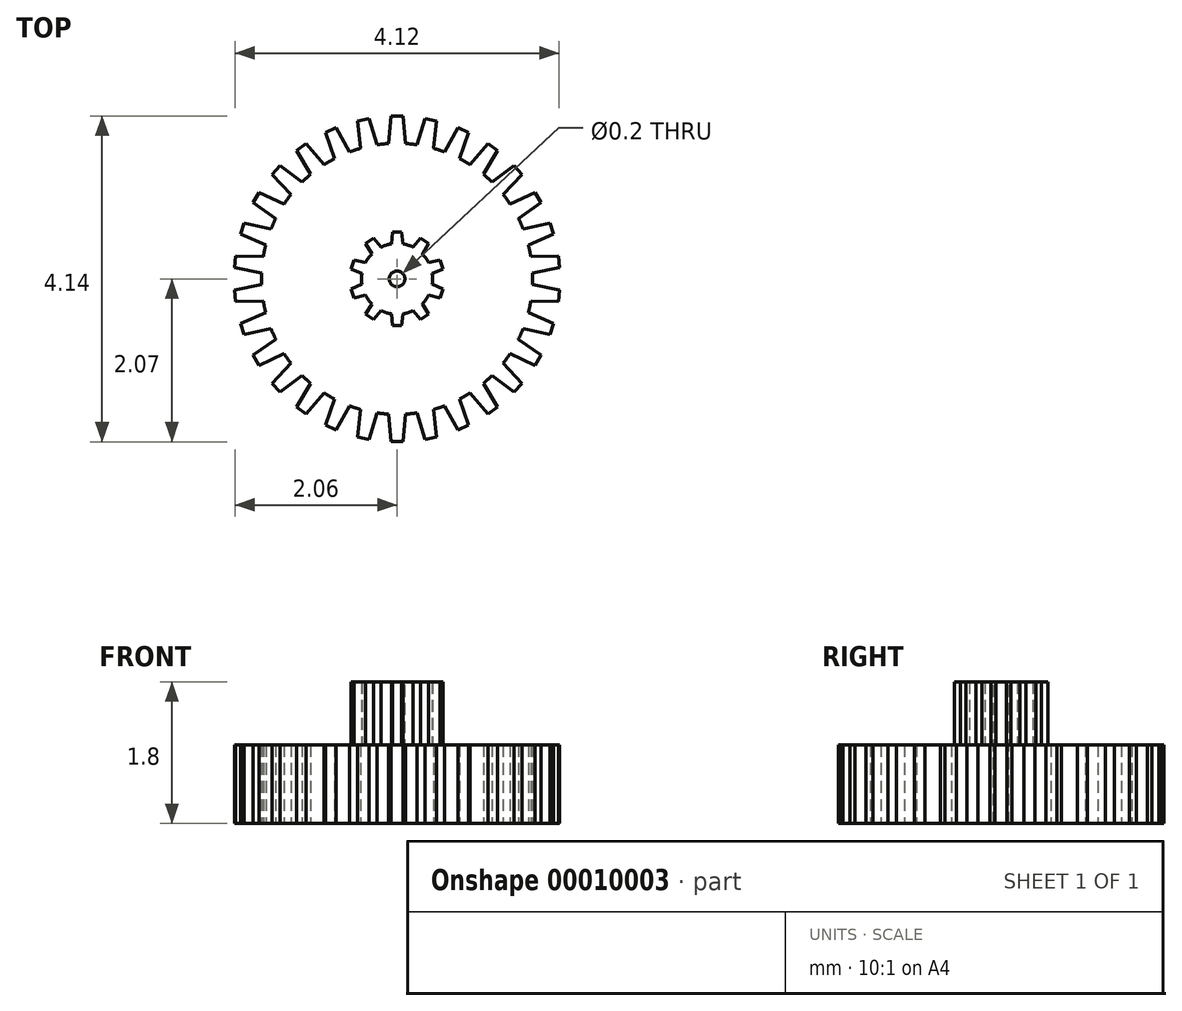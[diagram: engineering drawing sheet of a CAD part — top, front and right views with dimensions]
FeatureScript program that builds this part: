
annotation { "Feature Type Name" : "Feature", "Feature Type Description" : "" }
export const myFeature = defineFeature(function(context is Context, id is Id, definition is map)
    precondition{}
    {
        {
            var Q0;
            Q0=qCreatedBy(makeId("Top.planeOp"),FACE);
            var sketch = newSketch(context, id + "F0", { "sketchPlane" : qUnion([Q0])});
            skCircle(sketch, "E0", {"center": v(0, 0) * mm, "radius": 1.72 * mm});
            skLineSegment(sketch, "E1", {"start": v(0, 0) * mm, "end": v(0, 1.72) * mm, "construction": true});
            skLineSegment(sketch, "E2", {"start": v(-0.1, 1.72) * mm, "end": v(-0.08, 2.07) * mm});
            skLineSegment(sketch, "E3", {"start": v(-0.07, 2.07) * mm, "end": v(0, 2.07) * mm});
            skLineSegment(sketch, "E4.0.MirrorCS", {"start": v(0.07, 2.07) * mm, "end": v(0, 2.07) * mm});
            skLineSegment(sketch, "E5.0.MirrorCS", {"start": v(0.1, 1.72) * mm, "end": v(0.08, 2.07) * mm});
            skLineSegment(sketch, "E6.1.0", {"start": v(-0.46, 1.66) * mm, "end": v(-0.5, 2) * mm});
            skLineSegment(sketch, "E6.1.1", {"start": v(-0.5, 2) * mm, "end": v(-0.43, 2.02) * mm});
            skLineSegment(sketch, "E6.1.2", {"start": v(-0.36, 2.04) * mm, "end": v(-0.43, 2.02) * mm});
            skLineSegment(sketch, "E6.1.3", {"start": v(-0.25, 1.7) * mm, "end": v(-0.36, 2.04) * mm});
            skLineSegment(sketch, "E6.2.0", {"start": v(-0.8, 1.53) * mm, "end": v(-0.9, 1.86) * mm});
            skLineSegment(sketch, "E6.2.1", {"start": v(-0.9, 1.86) * mm, "end": v(-0.84, 1.89) * mm});
            skLineSegment(sketch, "E6.2.2", {"start": v(-0.77, 1.92) * mm, "end": v(-0.84, 1.89) * mm});
            skLineSegment(sketch, "E6.2.3", {"start": v(-0.6, 1.61) * mm, "end": v(-0.77, 1.92) * mm});
            skLineSegment(sketch, "E6.3.0", {"start": v(-1.1, 1.33) * mm, "end": v(-1.28, 1.63) * mm});
            skLineSegment(sketch, "E6.3.1", {"start": v(-1.28, 1.63) * mm, "end": v(-1.22, 1.67) * mm});
            skLineSegment(sketch, "E6.3.2", {"start": v(-1.15, 1.72) * mm, "end": v(-1.22, 1.67) * mm});
            skLineSegment(sketch, "E6.3.3", {"start": v(-0.92, 1.45) * mm, "end": v(-1.15, 1.72) * mm});
            skLineSegment(sketch, "E6.4.0", {"start": v(-1.35, 1.07) * mm, "end": v(-1.59, 1.33) * mm});
            skLineSegment(sketch, "E6.4.1", {"start": v(-1.59, 1.33) * mm, "end": v(-1.54, 1.38) * mm});
            skLineSegment(sketch, "E6.4.2", {"start": v(-1.49, 1.44) * mm, "end": v(-1.54, 1.38) * mm});
            skLineSegment(sketch, "E6.4.3", {"start": v(-1.2, 1.23) * mm, "end": v(-1.49, 1.44) * mm});
            skLineSegment(sketch, "E6.5.0", {"start": v(-1.54, 0.77) * mm, "end": v(-1.83, 0.97) * mm});
            skLineSegment(sketch, "E6.5.1", {"start": v(-1.83, 0.97) * mm, "end": v(-1.8, 1.03) * mm});
            skLineSegment(sketch, "E6.5.2", {"start": v(-1.75, 1.1) * mm, "end": v(-1.8, 1.03) * mm});
            skLineSegment(sketch, "E6.5.3", {"start": v(-1.44, 0.95) * mm, "end": v(-1.75, 1.1) * mm});
            skLineSegment(sketch, "E6.6.0", {"start": v(-1.67, 0.43) * mm, "end": v(-1.99, 0.57) * mm});
            skLineSegment(sketch, "E6.6.1", {"start": v(-1.99, 0.57) * mm, "end": v(-1.97, 0.64) * mm});
            skLineSegment(sketch, "E6.6.2", {"start": v(-1.94, 0.71) * mm, "end": v(-1.97, 0.64) * mm});
            skLineSegment(sketch, "E6.6.3", {"start": v(-1.6, 0.63) * mm, "end": v(-1.94, 0.71) * mm});
            skLineSegment(sketch, "E6.7.0", {"start": v(-1.72, 0.07) * mm, "end": v(-2.06, 0.14) * mm});
            skLineSegment(sketch, "E6.7.1", {"start": v(-2.06, 0.14) * mm, "end": v(-2.06, 0.22) * mm});
            skLineSegment(sketch, "E6.7.2", {"start": v(-2.05, 0.3) * mm, "end": v(-2.06, 0.22) * mm});
            skLineSegment(sketch, "E6.7.3", {"start": v(-1.7, 0.28) * mm, "end": v(-2.05, 0.3) * mm});
            skLineSegment(sketch, "E6.8.0", {"start": v(-1.7, -0.28) * mm, "end": v(-2.05, -0.3) * mm});
            skLineSegment(sketch, "E6.8.1", {"start": v(-2.05, -0.3) * mm, "end": v(-2.06, -0.22) * mm});
            skLineSegment(sketch, "E6.8.2", {"start": v(-2.06, -0.14) * mm, "end": v(-2.06, -0.22) * mm});
            skLineSegment(sketch, "E6.8.3", {"start": v(-1.72, -0.07) * mm, "end": v(-2.06, -0.14) * mm});
            skLineSegment(sketch, "E6.9.0", {"start": v(-1.6, -0.63) * mm, "end": v(-1.94, -0.71) * mm});
            skLineSegment(sketch, "E6.9.1", {"start": v(-1.94, -0.71) * mm, "end": v(-1.97, -0.64) * mm});
            skLineSegment(sketch, "E6.9.2", {"start": v(-1.99, -0.57) * mm, "end": v(-1.97, -0.64) * mm});
            skLineSegment(sketch, "E6.9.3", {"start": v(-1.67, -0.43) * mm, "end": v(-1.99, -0.57) * mm});
            skLineSegment(sketch, "E6.10.0", {"start": v(-1.44, -0.95) * mm, "end": v(-1.75, -1.1) * mm});
            skLineSegment(sketch, "E6.10.1", {"start": v(-1.75, -1.1) * mm, "end": v(-1.8, -1.03) * mm});
            skLineSegment(sketch, "E6.10.2", {"start": v(-1.83, -0.97) * mm, "end": v(-1.8, -1.03) * mm});
            skLineSegment(sketch, "E6.10.3", {"start": v(-1.54, -0.77) * mm, "end": v(-1.83, -0.97) * mm});
            skLineSegment(sketch, "E6.11.0", {"start": v(-1.2, -1.23) * mm, "end": v(-1.49, -1.44) * mm});
            skLineSegment(sketch, "E6.11.1", {"start": v(-1.49, -1.44) * mm, "end": v(-1.54, -1.38) * mm});
            skLineSegment(sketch, "E6.11.2", {"start": v(-1.59, -1.33) * mm, "end": v(-1.54, -1.38) * mm});
            skLineSegment(sketch, "E6.11.3", {"start": v(-1.35, -1.07) * mm, "end": v(-1.59, -1.33) * mm});
            skLineSegment(sketch, "E6.12.0", {"start": v(-0.92, -1.45) * mm, "end": v(-1.15, -1.72) * mm});
            skLineSegment(sketch, "E6.12.1", {"start": v(-1.15, -1.72) * mm, "end": v(-1.22, -1.67) * mm});
            skLineSegment(sketch, "E6.12.2", {"start": v(-1.28, -1.63) * mm, "end": v(-1.22, -1.67) * mm});
            skLineSegment(sketch, "E6.12.3", {"start": v(-1.1, -1.33) * mm, "end": v(-1.28, -1.63) * mm});
            skLineSegment(sketch, "E6.13.0", {"start": v(-0.6, -1.61) * mm, "end": v(-0.77, -1.92) * mm});
            skLineSegment(sketch, "E6.13.1", {"start": v(-0.77, -1.92) * mm, "end": v(-0.84, -1.89) * mm});
            skLineSegment(sketch, "E6.13.2", {"start": v(-0.9, -1.86) * mm, "end": v(-0.84, -1.89) * mm});
            skLineSegment(sketch, "E6.13.3", {"start": v(-0.8, -1.53) * mm, "end": v(-0.9, -1.86) * mm});
            skLineSegment(sketch, "E6.14.0", {"start": v(-0.25, -1.7) * mm, "end": v(-0.36, -2.04) * mm});
            skLineSegment(sketch, "E6.14.1", {"start": v(-0.36, -2.04) * mm, "end": v(-0.43, -2.02) * mm});
            skLineSegment(sketch, "E6.14.2", {"start": v(-0.5, -2) * mm, "end": v(-0.43, -2.02) * mm});
            skLineSegment(sketch, "E6.14.3", {"start": v(-0.46, -1.66) * mm, "end": v(-0.5, -2) * mm});
            skLineSegment(sketch, "E6.15.0", {"start": v(0.1, -1.72) * mm, "end": v(0.08, -2.07) * mm});
            skLineSegment(sketch, "E6.15.1", {"start": v(0.07, -2.07) * mm, "end": v(0, -2.07) * mm});
            skLineSegment(sketch, "E6.15.2", {"start": v(-0.07, -2.07) * mm, "end": v(0, -2.07) * mm});
            skLineSegment(sketch, "E6.15.3", {"start": v(-0.1, -1.72) * mm, "end": v(-0.08, -2.07) * mm});
            skLineSegment(sketch, "E6.16.0", {"start": v(0.46, -1.66) * mm, "end": v(0.5, -2) * mm});
            skLineSegment(sketch, "E6.16.1", {"start": v(0.5, -2) * mm, "end": v(0.43, -2.02) * mm});
            skLineSegment(sketch, "E6.16.2", {"start": v(0.36, -2.04) * mm, "end": v(0.43, -2.02) * mm});
            skLineSegment(sketch, "E6.16.3", {"start": v(0.25, -1.7) * mm, "end": v(0.36, -2.04) * mm});
            skLineSegment(sketch, "E6.17.0", {"start": v(0.8, -1.53) * mm, "end": v(0.9, -1.86) * mm});
            skLineSegment(sketch, "E6.17.1", {"start": v(0.9, -1.86) * mm, "end": v(0.84, -1.89) * mm});
            skLineSegment(sketch, "E6.17.2", {"start": v(0.77, -1.92) * mm, "end": v(0.84, -1.89) * mm});
            skLineSegment(sketch, "E6.17.3", {"start": v(0.6, -1.61) * mm, "end": v(0.77, -1.92) * mm});
            skLineSegment(sketch, "E6.18.0", {"start": v(1.1, -1.33) * mm, "end": v(1.28, -1.63) * mm});
            skLineSegment(sketch, "E6.18.1", {"start": v(1.28, -1.63) * mm, "end": v(1.22, -1.67) * mm});
            skLineSegment(sketch, "E6.18.2", {"start": v(1.15, -1.72) * mm, "end": v(1.22, -1.67) * mm});
            skLineSegment(sketch, "E6.18.3", {"start": v(0.92, -1.45) * mm, "end": v(1.15, -1.72) * mm});
            skLineSegment(sketch, "E6.19.0", {"start": v(1.35, -1.07) * mm, "end": v(1.59, -1.33) * mm});
            skLineSegment(sketch, "E6.19.1", {"start": v(1.59, -1.33) * mm, "end": v(1.54, -1.38) * mm});
            skLineSegment(sketch, "E6.19.2", {"start": v(1.49, -1.44) * mm, "end": v(1.54, -1.38) * mm});
            skLineSegment(sketch, "E6.19.3", {"start": v(1.2, -1.23) * mm, "end": v(1.49, -1.44) * mm});
            skLineSegment(sketch, "E6.20.0", {"start": v(1.54, -0.77) * mm, "end": v(1.83, -0.97) * mm});
            skLineSegment(sketch, "E6.20.1", {"start": v(1.83, -0.97) * mm, "end": v(1.8, -1.03) * mm});
            skLineSegment(sketch, "E6.20.2", {"start": v(1.75, -1.1) * mm, "end": v(1.8, -1.03) * mm});
            skLineSegment(sketch, "E6.20.3", {"start": v(1.44, -0.95) * mm, "end": v(1.75, -1.1) * mm});
            skLineSegment(sketch, "E7", {"start": v(0, 0) * mm, "end": v(0, 0.43) * mm, "construction": true});
            skLineSegment(sketch, "E8.1.21.0", {"start": v(1.67, -0.43) * mm, "end": v(1.99, -0.57) * mm});
            skLineSegment(sketch, "E8.3.21.0", {"start": v(1.99, -0.57) * mm, "end": v(1.97, -0.64) * mm});
            skLineSegment(sketch, "E8.6.21.0", {"start": v(1.94, -0.71) * mm, "end": v(1.97, -0.64) * mm});
            skLineSegment(sketch, "E8.9.21.0", {"start": v(1.6, -0.63) * mm, "end": v(1.94, -0.71) * mm});
            skLineSegment(sketch, "E8.1.22.0", {"start": v(1.72, -0.07) * mm, "end": v(2.06, -0.14) * mm});
            skLineSegment(sketch, "E8.3.22.0", {"start": v(2.06, -0.14) * mm, "end": v(2.06, -0.22) * mm});
            skLineSegment(sketch, "E8.6.22.0", {"start": v(2.05, -0.3) * mm, "end": v(2.06, -0.22) * mm});
            skLineSegment(sketch, "E8.9.22.0", {"start": v(1.7, -0.28) * mm, "end": v(2.05, -0.3) * mm});
            skLineSegment(sketch, "E8.1.23.0", {"start": v(1.7, 0.28) * mm, "end": v(2.05, 0.3) * mm});
            skLineSegment(sketch, "E8.3.23.0", {"start": v(2.05, 0.3) * mm, "end": v(2.06, 0.22) * mm});
            skLineSegment(sketch, "E8.6.23.0", {"start": v(2.06, 0.14) * mm, "end": v(2.06, 0.22) * mm});
            skLineSegment(sketch, "E8.9.23.0", {"start": v(1.72, 0.07) * mm, "end": v(2.06, 0.14) * mm});
            skLineSegment(sketch, "E9.1.24.0", {"start": v(1.6, 0.63) * mm, "end": v(1.94, 0.71) * mm});
            skLineSegment(sketch, "E9.3.24.0", {"start": v(1.94, 0.71) * mm, "end": v(1.97, 0.64) * mm});
            skLineSegment(sketch, "E9.6.24.0", {"start": v(1.99, 0.57) * mm, "end": v(1.97, 0.64) * mm});
            skLineSegment(sketch, "E9.9.24.0", {"start": v(1.67, 0.43) * mm, "end": v(1.99, 0.57) * mm});
            skLineSegment(sketch, "E9.1.25.0", {"start": v(1.44, 0.95) * mm, "end": v(1.75, 1.1) * mm});
            skLineSegment(sketch, "E9.3.25.0", {"start": v(1.75, 1.1) * mm, "end": v(1.8, 1.03) * mm});
            skLineSegment(sketch, "E9.6.25.0", {"start": v(1.83, 0.97) * mm, "end": v(1.8, 1.03) * mm});
            skLineSegment(sketch, "E9.9.25.0", {"start": v(1.54, 0.77) * mm, "end": v(1.83, 0.97) * mm});
            skLineSegment(sketch, "E9.1.26.0", {"start": v(1.2, 1.23) * mm, "end": v(1.49, 1.44) * mm});
            skLineSegment(sketch, "E9.3.26.0", {"start": v(1.49, 1.44) * mm, "end": v(1.54, 1.38) * mm});
            skLineSegment(sketch, "E9.6.26.0", {"start": v(1.59, 1.33) * mm, "end": v(1.54, 1.38) * mm});
            skLineSegment(sketch, "E9.9.26.0", {"start": v(1.35, 1.07) * mm, "end": v(1.59, 1.33) * mm});
            skLineSegment(sketch, "E9.1.27.0", {"start": v(0.92, 1.45) * mm, "end": v(1.15, 1.72) * mm});
            skLineSegment(sketch, "E9.3.27.0", {"start": v(1.15, 1.72) * mm, "end": v(1.22, 1.67) * mm});
            skLineSegment(sketch, "E9.6.27.0", {"start": v(1.28, 1.63) * mm, "end": v(1.22, 1.67) * mm});
            skLineSegment(sketch, "E9.9.27.0", {"start": v(1.1, 1.33) * mm, "end": v(1.28, 1.63) * mm});
            skLineSegment(sketch, "E9.1.28.0", {"start": v(0.6, 1.61) * mm, "end": v(0.77, 1.92) * mm});
            skLineSegment(sketch, "E9.3.28.0", {"start": v(0.77, 1.92) * mm, "end": v(0.84, 1.89) * mm});
            skLineSegment(sketch, "E9.6.28.0", {"start": v(0.9, 1.86) * mm, "end": v(0.84, 1.89) * mm});
            skLineSegment(sketch, "E9.9.28.0", {"start": v(0.8, 1.53) * mm, "end": v(0.9, 1.86) * mm});
            skLineSegment(sketch, "E9.1.29.0", {"start": v(0.25, 1.7) * mm, "end": v(0.36, 2.04) * mm});
            skLineSegment(sketch, "E9.3.29.0", {"start": v(0.36, 2.04) * mm, "end": v(0.43, 2.02) * mm});
            skLineSegment(sketch, "E9.6.29.0", {"start": v(0.5, 2) * mm, "end": v(0.43, 2.02) * mm});
            skLineSegment(sketch, "E9.9.29.0", {"start": v(0.46, 1.66) * mm, "end": v(0.5, 2) * mm});
            skSolve(sketch);
        }
        {
            var Q0;
            Q0=qSketchRegion(id+"F0",true);
            extrude(context, id + "F1", {"entities" : qUnion([Q0]), "depth" : 1 * mm});
        }
        {
            var Q0;
            Q0=makeQuery(id+"F1.opExtrude","CAP_FACE",FACE,{"disambiguationData":[OSD([sQuery(id+"F0.wireOp",EDGE,"E0"),sQuery(id+"F0.wireOp",EDGE,"E2"),sQuery(id+"F0.wireOp",EDGE,"E3"),sQuery(id+"F0.wireOp",EDGE,"E4.0.MirrorCS"),sQuery(id+"F0.wireOp",EDGE,"E5.0.MirrorCS"),sQuery(id+"F0.wireOp",EDGE,"E6.1.0"),sQuery(id+"F0.wireOp",EDGE,"E6.1.1"),sQuery(id+"F0.wireOp",EDGE,"E6.1.2"),sQuery(id+"F0.wireOp",EDGE,"E6.1.3"),sQuery(id+"F0.wireOp",EDGE,"E6.2.0"),sQuery(id+"F0.wireOp",EDGE,"E6.2.1"),sQuery(id+"F0.wireOp",EDGE,"E6.2.2"),sQuery(id+"F0.wireOp",EDGE,"E6.2.3"),sQuery(id+"F0.wireOp",EDGE,"E6.3.0"),sQuery(id+"F0.wireOp",EDGE,"E6.3.1"),sQuery(id+"F0.wireOp",EDGE,"E6.3.2"),sQuery(id+"F0.wireOp",EDGE,"E6.3.3"),sQuery(id+"F0.wireOp",EDGE,"E6.4.0"),sQuery(id+"F0.wireOp",EDGE,"E6.4.1"),sQuery(id+"F0.wireOp",EDGE,"E6.4.2"),sQuery(id+"F0.wireOp",EDGE,"E6.4.3"),sQuery(id+"F0.wireOp",EDGE,"E6.5.0"),sQuery(id+"F0.wireOp",EDGE,"E6.5.1"),sQuery(id+"F0.wireOp",EDGE,"E6.5.2"),sQuery(id+"F0.wireOp",EDGE,"E6.5.3"),sQuery(id+"F0.wireOp",EDGE,"E6.6.0"),sQuery(id+"F0.wireOp",EDGE,"E6.6.1"),sQuery(id+"F0.wireOp",EDGE,"E6.6.2"),sQuery(id+"F0.wireOp",EDGE,"E6.6.3"),sQuery(id+"F0.wireOp",EDGE,"E6.7.0"),sQuery(id+"F0.wireOp",EDGE,"E6.7.1"),sQuery(id+"F0.wireOp",EDGE,"E6.7.2"),sQuery(id+"F0.wireOp",EDGE,"E6.7.3"),sQuery(id+"F0.wireOp",EDGE,"E6.8.0"),sQuery(id+"F0.wireOp",EDGE,"E6.8.1"),sQuery(id+"F0.wireOp",EDGE,"E6.8.2"),sQuery(id+"F0.wireOp",EDGE,"E6.8.3"),sQuery(id+"F0.wireOp",EDGE,"E6.9.0"),sQuery(id+"F0.wireOp",EDGE,"E6.9.1"),sQuery(id+"F0.wireOp",EDGE,"E6.9.2"),sQuery(id+"F0.wireOp",EDGE,"E6.9.3"),sQuery(id+"F0.wireOp",EDGE,"E6.10.0"),sQuery(id+"F0.wireOp",EDGE,"E6.10.1"),sQuery(id+"F0.wireOp",EDGE,"E6.10.2"),sQuery(id+"F0.wireOp",EDGE,"E6.10.3"),sQuery(id+"F0.wireOp",EDGE,"E6.11.0"),sQuery(id+"F0.wireOp",EDGE,"E6.11.1"),sQuery(id+"F0.wireOp",EDGE,"E6.11.2"),sQuery(id+"F0.wireOp",EDGE,"E6.11.3"),sQuery(id+"F0.wireOp",EDGE,"E6.12.0"),sQuery(id+"F0.wireOp",EDGE,"E6.12.1"),sQuery(id+"F0.wireOp",EDGE,"E6.12.2"),sQuery(id+"F0.wireOp",EDGE,"E6.12.3"),sQuery(id+"F0.wireOp",EDGE,"E6.13.0"),sQuery(id+"F0.wireOp",EDGE,"E6.13.1"),sQuery(id+"F0.wireOp",EDGE,"E6.13.2"),sQuery(id+"F0.wireOp",EDGE,"E6.13.3"),sQuery(id+"F0.wireOp",EDGE,"E6.14.0"),sQuery(id+"F0.wireOp",EDGE,"E6.14.1"),sQuery(id+"F0.wireOp",EDGE,"E6.14.2"),sQuery(id+"F0.wireOp",EDGE,"E6.14.3"),sQuery(id+"F0.wireOp",EDGE,"E6.15.0"),sQuery(id+"F0.wireOp",EDGE,"E6.15.1"),sQuery(id+"F0.wireOp",EDGE,"E6.15.2"),sQuery(id+"F0.wireOp",EDGE,"E6.15.3"),sQuery(id+"F0.wireOp",EDGE,"E6.16.0"),sQuery(id+"F0.wireOp",EDGE,"E6.16.1"),sQuery(id+"F0.wireOp",EDGE,"E6.16.2"),sQuery(id+"F0.wireOp",EDGE,"E6.16.3"),sQuery(id+"F0.wireOp",EDGE,"E6.17.0"),sQuery(id+"F0.wireOp",EDGE,"E6.17.1"),sQuery(id+"F0.wireOp",EDGE,"E6.17.2"),sQuery(id+"F0.wireOp",EDGE,"E6.17.3"),sQuery(id+"F0.wireOp",EDGE,"E6.18.0"),sQuery(id+"F0.wireOp",EDGE,"E6.18.1"),sQuery(id+"F0.wireOp",EDGE,"E6.18.2"),sQuery(id+"F0.wireOp",EDGE,"E6.18.3"),sQuery(id+"F0.wireOp",EDGE,"E6.19.0"),sQuery(id+"F0.wireOp",EDGE,"E6.19.1"),sQuery(id+"F0.wireOp",EDGE,"E6.19.2"),sQuery(id+"F0.wireOp",EDGE,"E6.19.3"),sQuery(id+"F0.wireOp",EDGE,"E6.20.0"),sQuery(id+"F0.wireOp",EDGE,"E6.20.1"),sQuery(id+"F0.wireOp",EDGE,"E6.20.2"),sQuery(id+"F0.wireOp",EDGE,"E6.20.3"),sQuery(id+"F0.wireOp",EDGE,"E6.21.0"),sQuery(id+"F0.wireOp",EDGE,"E6.21.1"),sQuery(id+"F0.wireOp",EDGE,"E6.21.2"),sQuery(id+"F0.wireOp",EDGE,"E6.21.3"),sQuery(id+"F0.wireOp",EDGE,"E6.22.0"),sQuery(id+"F0.wireOp",EDGE,"E6.22.1"),sQuery(id+"F0.wireOp",EDGE,"E6.22.2"),sQuery(id+"F0.wireOp",EDGE,"E6.22.3"),sQuery(id+"F0.wireOp",EDGE,"E6.23.0"),sQuery(id+"F0.wireOp",EDGE,"E6.23.1"),sQuery(id+"F0.wireOp",EDGE,"E6.23.2"),sQuery(id+"F0.wireOp",EDGE,"E6.23.3"),sQuery(id+"F0.wireOp",EDGE,"E6.24.0"),sQuery(id+"F0.wireOp",EDGE,"E6.24.1"),sQuery(id+"F0.wireOp",EDGE,"E6.24.2"),sQuery(id+"F0.wireOp",EDGE,"E6.24.3"),sQuery(id+"F0.wireOp",EDGE,"E6.25.0"),sQuery(id+"F0.wireOp",EDGE,"E6.25.1"),sQuery(id+"F0.wireOp",EDGE,"E6.25.2"),sQuery(id+"F0.wireOp",EDGE,"E6.25.3"),sQuery(id+"F0.wireOp",EDGE,"E6.26.0"),sQuery(id+"F0.wireOp",EDGE,"E6.26.1"),sQuery(id+"F0.wireOp",EDGE,"E6.26.2"),sQuery(id+"F0.wireOp",EDGE,"E6.26.3"),sQuery(id+"F0.wireOp",EDGE,"E6.27.0"),sQuery(id+"F0.wireOp",EDGE,"E6.27.1"),sQuery(id+"F0.wireOp",EDGE,"E6.27.2"),sQuery(id+"F0.wireOp",EDGE,"E6.27.3"),sQuery(id+"F0.wireOp",EDGE,"E6.28.0"),sQuery(id+"F0.wireOp",EDGE,"E6.28.1"),sQuery(id+"F0.wireOp",EDGE,"E6.28.2"),sQuery(id+"F0.wireOp",EDGE,"E6.28.3"),sQuery(id+"F0.wireOp",EDGE,"E6.29.0"),sQuery(id+"F0.wireOp",EDGE,"E6.29.1"),sQuery(id+"F0.wireOp",EDGE,"E6.29.2"),sQuery(id+"F0.wireOp",EDGE,"E6.29.3"),sQuery(id+"F0.wireOp",EDGE,"E6.30.0"),sQuery(id+"F0.wireOp",EDGE,"E6.30.1"),sQuery(id+"F0.wireOp",EDGE,"E6.30.2"),sQuery(id+"F0.wireOp",EDGE,"E6.30.3"),sQuery(id+"F0.wireOp",EDGE,"E6.31.0"),sQuery(id+"F0.wireOp",EDGE,"E6.31.1"),sQuery(id+"F0.wireOp",EDGE,"E6.31.2"),sQuery(id+"F0.wireOp",EDGE,"E6.31.3"),sQuery(id+"F0.wireOp",EDGE,"E6.32.0"),sQuery(id+"F0.wireOp",EDGE,"E6.32.1"),sQuery(id+"F0.wireOp",EDGE,"E6.32.2"),sQuery(id+"F0.wireOp",EDGE,"E6.32.3"),sQuery(id+"F0.wireOp",EDGE,"E6.33.0"),sQuery(id+"F0.wireOp",EDGE,"E6.33.1"),sQuery(id+"F0.wireOp",EDGE,"E6.33.2"),sQuery(id+"F0.wireOp",EDGE,"E6.33.3"),sQuery(id+"F0.wireOp",EDGE,"E6.34.0"),sQuery(id+"F0.wireOp",EDGE,"E6.34.1"),sQuery(id+"F0.wireOp",EDGE,"E6.34.2"),sQuery(id+"F0.wireOp",EDGE,"E6.34.3"),sQuery(id+"F0.wireOp",EDGE,"E6.35.0"),sQuery(id+"F0.wireOp",EDGE,"E6.35.1"),sQuery(id+"F0.wireOp",EDGE,"E6.35.2"),sQuery(id+"F0.wireOp",EDGE,"E6.35.3"),sQuery(id+"F0.wireOp",EDGE,"E6.36.0"),sQuery(id+"F0.wireOp",EDGE,"E6.36.1"),sQuery(id+"F0.wireOp",EDGE,"E6.36.2"),sQuery(id+"F0.wireOp",EDGE,"E6.36.3"),sQuery(id+"F0.wireOp",EDGE,"E6.37.0"),sQuery(id+"F0.wireOp",EDGE,"E6.37.1"),sQuery(id+"F0.wireOp",EDGE,"E6.37.2"),sQuery(id+"F0.wireOp",EDGE,"E6.37.3"),sQuery(id+"F0.wireOp",EDGE,"E6.38.0"),sQuery(id+"F0.wireOp",EDGE,"E6.38.1"),sQuery(id+"F0.wireOp",EDGE,"E6.38.2"),sQuery(id+"F0.wireOp",EDGE,"E6.38.3"),sQuery(id+"F0.wireOp",EDGE,"E6.39.0"),sQuery(id+"F0.wireOp",EDGE,"E6.39.1"),sQuery(id+"F0.wireOp",EDGE,"E6.39.2"),sQuery(id+"F0.wireOp",EDGE,"E6.39.3"),sQuery(id+"F0.wireOp",EDGE,"E6.40.0"),sQuery(id+"F0.wireOp",EDGE,"E6.40.1"),sQuery(id+"F0.wireOp",EDGE,"E6.40.2"),sQuery(id+"F0.wireOp",EDGE,"E6.40.3"),sQuery(id+"F0.wireOp",EDGE,"E6.41.0"),sQuery(id+"F0.wireOp",EDGE,"E6.41.1"),sQuery(id+"F0.wireOp",EDGE,"E6.41.2"),sQuery(id+"F0.wireOp",EDGE,"E6.41.3"),sQuery(id+"F0.wireOp",EDGE,"E6.42.0"),sQuery(id+"F0.wireOp",EDGE,"E6.42.1"),sQuery(id+"F0.wireOp",EDGE,"E6.42.2"),sQuery(id+"F0.wireOp",EDGE,"E6.42.3"),sQuery(id+"F0.wireOp",EDGE,"E6.43.0"),sQuery(id+"F0.wireOp",EDGE,"E6.43.1"),sQuery(id+"F0.wireOp",EDGE,"E6.43.2"),sQuery(id+"F0.wireOp",EDGE,"E6.43.3"),sQuery(id+"F0.wireOp",EDGE,"E6.44.0"),sQuery(id+"F0.wireOp",EDGE,"E6.44.1"),sQuery(id+"F0.wireOp",EDGE,"E6.44.2"),sQuery(id+"F0.wireOp",EDGE,"E6.44.3"),sQuery(id+"F0.wireOp",EDGE,"E6.45.0"),sQuery(id+"F0.wireOp",EDGE,"E6.45.1"),sQuery(id+"F0.wireOp",EDGE,"E6.45.2"),sQuery(id+"F0.wireOp",EDGE,"E6.45.3"),sQuery(id+"F0.wireOp",EDGE,"E6.46.0"),sQuery(id+"F0.wireOp",EDGE,"E6.46.1"),sQuery(id+"F0.wireOp",EDGE,"E6.46.2"),sQuery(id+"F0.wireOp",EDGE,"E6.46.3"),sQuery(id+"F0.wireOp",EDGE,"E6.47.0"),sQuery(id+"F0.wireOp",EDGE,"E6.47.1"),sQuery(id+"F0.wireOp",EDGE,"E6.47.2"),sQuery(id+"F0.wireOp",EDGE,"E6.47.3"),sQuery(id+"F0.wireOp",EDGE,"E6.48.0"),sQuery(id+"F0.wireOp",EDGE,"E6.48.1"),sQuery(id+"F0.wireOp",EDGE,"E6.48.2"),sQuery(id+"F0.wireOp",EDGE,"E6.48.3"),sQuery(id+"F0.wireOp",EDGE,"E6.49.0"),sQuery(id+"F0.wireOp",EDGE,"E6.49.1"),sQuery(id+"F0.wireOp",EDGE,"E6.49.2"),sQuery(id+"F0.wireOp",EDGE,"E6.49.3"),sQuery(id+"F0.wireOp",EDGE,"E6.50.0"),sQuery(id+"F0.wireOp",EDGE,"E6.50.1"),sQuery(id+"F0.wireOp",EDGE,"E6.50.2"),sQuery(id+"F0.wireOp",EDGE,"E6.50.3"),sQuery(id+"F0.wireOp",EDGE,"E6.51.0"),sQuery(id+"F0.wireOp",EDGE,"E6.51.1"),sQuery(id+"F0.wireOp",EDGE,"E6.51.2"),sQuery(id+"F0.wireOp",EDGE,"E6.51.3"),sQuery(id+"F0.wireOp",EDGE,"E6.52.0"),sQuery(id+"F0.wireOp",EDGE,"E6.52.1"),sQuery(id+"F0.wireOp",EDGE,"E6.52.2"),sQuery(id+"F0.wireOp",EDGE,"E6.52.3"),sQuery(id+"F0.wireOp",EDGE,"E6.53.0"),sQuery(id+"F0.wireOp",EDGE,"E6.53.1"),sQuery(id+"F0.wireOp",EDGE,"E6.53.2"),sQuery(id+"F0.wireOp",EDGE,"E6.53.3"),sQuery(id+"F0.wireOp",EDGE,"E6.54.0"),sQuery(id+"F0.wireOp",EDGE,"E6.54.1"),sQuery(id+"F0.wireOp",EDGE,"E6.54.2"),sQuery(id+"F0.wireOp",EDGE,"E6.54.3"),sQuery(id+"F0.wireOp",EDGE,"E6.55.0"),sQuery(id+"F0.wireOp",EDGE,"E6.55.1"),sQuery(id+"F0.wireOp",EDGE,"E6.55.2"),sQuery(id+"F0.wireOp",EDGE,"E6.55.3"),sQuery(id+"F0.wireOp",EDGE,"E6.56.0"),sQuery(id+"F0.wireOp",EDGE,"E6.56.1"),sQuery(id+"F0.wireOp",EDGE,"E6.56.2"),sQuery(id+"F0.wireOp",EDGE,"E6.56.3"),sQuery(id+"F0.wireOp",EDGE,"E6.57.0"),sQuery(id+"F0.wireOp",EDGE,"E6.57.1"),sQuery(id+"F0.wireOp",EDGE,"E6.57.2"),sQuery(id+"F0.wireOp",EDGE,"E6.57.3"),sQuery(id+"F0.wireOp",EDGE,"E6.58.0"),sQuery(id+"F0.wireOp",EDGE,"E6.58.1"),sQuery(id+"F0.wireOp",EDGE,"E6.58.2"),sQuery(id+"F0.wireOp",EDGE,"E6.58.3"),sQuery(id+"F0.wireOp",EDGE,"E6.59.0"),sQuery(id+"F0.wireOp",EDGE,"E6.59.1"),sQuery(id+"F0.wireOp",EDGE,"E6.59.2"),sQuery(id+"F0.wireOp",EDGE,"E6.59.3"),sQuery(id+"F0.wireOp",EDGE,"E6.60.0"),sQuery(id+"F0.wireOp",EDGE,"E6.60.1"),sQuery(id+"F0.wireOp",EDGE,"E6.60.2"),sQuery(id+"F0.wireOp",EDGE,"E6.60.3"),sQuery(id+"F0.wireOp",EDGE,"E6.61.0"),sQuery(id+"F0.wireOp",EDGE,"E6.61.1"),sQuery(id+"F0.wireOp",EDGE,"E6.61.2"),sQuery(id+"F0.wireOp",EDGE,"E6.61.3"),sQuery(id+"F0.wireOp",EDGE,"E6.62.0"),sQuery(id+"F0.wireOp",EDGE,"E6.62.1"),sQuery(id+"F0.wireOp",EDGE,"E6.62.2"),sQuery(id+"F0.wireOp",EDGE,"E6.62.3"),sQuery(id+"F0.wireOp",EDGE,"E6.63.0"),sQuery(id+"F0.wireOp",EDGE,"E6.63.1"),sQuery(id+"F0.wireOp",EDGE,"E6.63.2"),sQuery(id+"F0.wireOp",EDGE,"E6.63.3"),sQuery(id+"F0.wireOp",EDGE,"E6.64.0"),sQuery(id+"F0.wireOp",EDGE,"E6.64.1"),sQuery(id+"F0.wireOp",EDGE,"E6.64.2"),sQuery(id+"F0.wireOp",EDGE,"E6.64.3"),sQuery(id+"F0.wireOp",EDGE,"E6.65.0"),sQuery(id+"F0.wireOp",EDGE,"E6.65.1"),sQuery(id+"F0.wireOp",EDGE,"E6.65.2"),sQuery(id+"F0.wireOp",EDGE,"E6.65.3"),sQuery(id+"F0.wireOp",EDGE,"E6.66.0"),sQuery(id+"F0.wireOp",EDGE,"E6.66.1"),sQuery(id+"F0.wireOp",EDGE,"E6.66.2"),sQuery(id+"F0.wireOp",EDGE,"E6.66.3"),sQuery(id+"F0.wireOp",EDGE,"E6.67.0"),sQuery(id+"F0.wireOp",EDGE,"E6.67.1"),sQuery(id+"F0.wireOp",EDGE,"E6.67.2"),sQuery(id+"F0.wireOp",EDGE,"E6.67.3"),sQuery(id+"F0.wireOp",EDGE,"E6.68.0"),sQuery(id+"F0.wireOp",EDGE,"E6.68.1"),sQuery(id+"F0.wireOp",EDGE,"E6.68.2"),sQuery(id+"F0.wireOp",EDGE,"E6.68.3"),sQuery(id+"F0.wireOp",EDGE,"E6.69.0"),sQuery(id+"F0.wireOp",EDGE,"E6.69.1"),sQuery(id+"F0.wireOp",EDGE,"E6.69.2"),sQuery(id+"F0.wireOp",EDGE,"E6.69.3"),sQuery(id+"F0.wireOp",EDGE,"E6.70.0"),sQuery(id+"F0.wireOp",EDGE,"E6.70.1"),sQuery(id+"F0.wireOp",EDGE,"E6.70.2"),sQuery(id+"F0.wireOp",EDGE,"E6.70.3"),sQuery(id+"F0.wireOp",EDGE,"E6.71.0"),sQuery(id+"F0.wireOp",EDGE,"E6.71.1"),sQuery(id+"F0.wireOp",EDGE,"E6.71.2"),sQuery(id+"F0.wireOp",EDGE,"E6.71.3")])],"isStart":false});
            var sketch = newSketch(context, id + "F2", { "sketchPlane" : qUnion([Q0])});
            skCircle(sketch, "E10", {"center": v(0, 0) * mm, "radius": 0.1 * mm});
            skSolve(sketch);
        }
        {
            var Q0;
            Q0=qSketchRegion(id+"F2",true);
            extrude(context, id + "F3", {"entities" : qUnion([Q0]), "operationType" : NewBodyOperationType.REMOVE, "oppositeDirection" : true, "depth" : 25 * mm});
        }
        {
            var Q0;
            Q0=makeQuery(id+"F1.opExtrude","CAP_FACE",FACE,{"disambiguationData":[OSD([sQuery(id+"F0.wireOp",EDGE,"E0"),sQuery(id+"F0.wireOp",EDGE,"E2"),sQuery(id+"F0.wireOp",EDGE,"E3"),sQuery(id+"F0.wireOp",EDGE,"E4.0.MirrorCS"),sQuery(id+"F0.wireOp",EDGE,"E5.0.MirrorCS"),sQuery(id+"F0.wireOp",EDGE,"E6.1.0"),sQuery(id+"F0.wireOp",EDGE,"E6.1.1"),sQuery(id+"F0.wireOp",EDGE,"E6.1.2"),sQuery(id+"F0.wireOp",EDGE,"E6.1.3"),sQuery(id+"F0.wireOp",EDGE,"E6.2.0"),sQuery(id+"F0.wireOp",EDGE,"E6.2.1"),sQuery(id+"F0.wireOp",EDGE,"E6.2.2"),sQuery(id+"F0.wireOp",EDGE,"E6.2.3"),sQuery(id+"F0.wireOp",EDGE,"E6.3.0"),sQuery(id+"F0.wireOp",EDGE,"E6.3.1"),sQuery(id+"F0.wireOp",EDGE,"E6.3.2"),sQuery(id+"F0.wireOp",EDGE,"E6.3.3"),sQuery(id+"F0.wireOp",EDGE,"E6.4.0"),sQuery(id+"F0.wireOp",EDGE,"E6.4.1"),sQuery(id+"F0.wireOp",EDGE,"E6.4.2"),sQuery(id+"F0.wireOp",EDGE,"E6.4.3"),sQuery(id+"F0.wireOp",EDGE,"E6.5.0"),sQuery(id+"F0.wireOp",EDGE,"E6.5.1"),sQuery(id+"F0.wireOp",EDGE,"E6.5.2"),sQuery(id+"F0.wireOp",EDGE,"E6.5.3"),sQuery(id+"F0.wireOp",EDGE,"E6.6.0"),sQuery(id+"F0.wireOp",EDGE,"E6.6.1"),sQuery(id+"F0.wireOp",EDGE,"E6.6.2"),sQuery(id+"F0.wireOp",EDGE,"E6.6.3"),sQuery(id+"F0.wireOp",EDGE,"E6.7.0"),sQuery(id+"F0.wireOp",EDGE,"E6.7.1"),sQuery(id+"F0.wireOp",EDGE,"E6.7.2"),sQuery(id+"F0.wireOp",EDGE,"E6.7.3"),sQuery(id+"F0.wireOp",EDGE,"E6.8.0"),sQuery(id+"F0.wireOp",EDGE,"E6.8.1"),sQuery(id+"F0.wireOp",EDGE,"E6.8.2"),sQuery(id+"F0.wireOp",EDGE,"E6.8.3"),sQuery(id+"F0.wireOp",EDGE,"E6.9.0"),sQuery(id+"F0.wireOp",EDGE,"E6.9.1"),sQuery(id+"F0.wireOp",EDGE,"E6.9.2"),sQuery(id+"F0.wireOp",EDGE,"E6.9.3"),sQuery(id+"F0.wireOp",EDGE,"E6.10.0"),sQuery(id+"F0.wireOp",EDGE,"E6.10.1"),sQuery(id+"F0.wireOp",EDGE,"E6.10.2"),sQuery(id+"F0.wireOp",EDGE,"E6.10.3"),sQuery(id+"F0.wireOp",EDGE,"E6.11.0"),sQuery(id+"F0.wireOp",EDGE,"E6.11.1"),sQuery(id+"F0.wireOp",EDGE,"E6.11.2"),sQuery(id+"F0.wireOp",EDGE,"E6.11.3"),sQuery(id+"F0.wireOp",EDGE,"E6.12.0"),sQuery(id+"F0.wireOp",EDGE,"E6.12.1"),sQuery(id+"F0.wireOp",EDGE,"E6.12.2"),sQuery(id+"F0.wireOp",EDGE,"E6.12.3"),sQuery(id+"F0.wireOp",EDGE,"E6.13.0"),sQuery(id+"F0.wireOp",EDGE,"E6.13.1"),sQuery(id+"F0.wireOp",EDGE,"E6.13.2"),sQuery(id+"F0.wireOp",EDGE,"E6.13.3"),sQuery(id+"F0.wireOp",EDGE,"E6.14.0"),sQuery(id+"F0.wireOp",EDGE,"E6.14.1"),sQuery(id+"F0.wireOp",EDGE,"E6.14.2"),sQuery(id+"F0.wireOp",EDGE,"E6.14.3"),sQuery(id+"F0.wireOp",EDGE,"E6.15.0"),sQuery(id+"F0.wireOp",EDGE,"E6.15.1"),sQuery(id+"F0.wireOp",EDGE,"E6.15.2"),sQuery(id+"F0.wireOp",EDGE,"E6.15.3"),sQuery(id+"F0.wireOp",EDGE,"E6.16.0"),sQuery(id+"F0.wireOp",EDGE,"E6.16.1"),sQuery(id+"F0.wireOp",EDGE,"E6.16.2"),sQuery(id+"F0.wireOp",EDGE,"E6.16.3"),sQuery(id+"F0.wireOp",EDGE,"E6.17.0"),sQuery(id+"F0.wireOp",EDGE,"E6.17.1"),sQuery(id+"F0.wireOp",EDGE,"E6.17.2"),sQuery(id+"F0.wireOp",EDGE,"E6.17.3"),sQuery(id+"F0.wireOp",EDGE,"E6.18.0"),sQuery(id+"F0.wireOp",EDGE,"E6.18.1"),sQuery(id+"F0.wireOp",EDGE,"E6.18.2"),sQuery(id+"F0.wireOp",EDGE,"E6.18.3"),sQuery(id+"F0.wireOp",EDGE,"E6.19.0"),sQuery(id+"F0.wireOp",EDGE,"E6.19.1"),sQuery(id+"F0.wireOp",EDGE,"E6.19.2"),sQuery(id+"F0.wireOp",EDGE,"E6.19.3"),sQuery(id+"F0.wireOp",EDGE,"E6.20.0"),sQuery(id+"F0.wireOp",EDGE,"E6.20.1"),sQuery(id+"F0.wireOp",EDGE,"E6.20.2"),sQuery(id+"F0.wireOp",EDGE,"E6.20.3"),sQuery(id+"F0.wireOp",EDGE,"E6.21.0"),sQuery(id+"F0.wireOp",EDGE,"E6.21.1"),sQuery(id+"F0.wireOp",EDGE,"E6.21.2"),sQuery(id+"F0.wireOp",EDGE,"E6.21.3"),sQuery(id+"F0.wireOp",EDGE,"E6.22.0"),sQuery(id+"F0.wireOp",EDGE,"E6.22.1"),sQuery(id+"F0.wireOp",EDGE,"E6.22.2"),sQuery(id+"F0.wireOp",EDGE,"E6.22.3"),sQuery(id+"F0.wireOp",EDGE,"E6.23.0"),sQuery(id+"F0.wireOp",EDGE,"E6.23.1"),sQuery(id+"F0.wireOp",EDGE,"E6.23.2"),sQuery(id+"F0.wireOp",EDGE,"E6.23.3"),sQuery(id+"F0.wireOp",EDGE,"E6.24.0"),sQuery(id+"F0.wireOp",EDGE,"E6.24.1"),sQuery(id+"F0.wireOp",EDGE,"E6.24.2"),sQuery(id+"F0.wireOp",EDGE,"E6.24.3"),sQuery(id+"F0.wireOp",EDGE,"E6.25.0"),sQuery(id+"F0.wireOp",EDGE,"E6.25.1"),sQuery(id+"F0.wireOp",EDGE,"E6.25.2"),sQuery(id+"F0.wireOp",EDGE,"E6.25.3"),sQuery(id+"F0.wireOp",EDGE,"E6.26.0"),sQuery(id+"F0.wireOp",EDGE,"E6.26.1"),sQuery(id+"F0.wireOp",EDGE,"E6.26.2"),sQuery(id+"F0.wireOp",EDGE,"E6.26.3"),sQuery(id+"F0.wireOp",EDGE,"E6.27.0"),sQuery(id+"F0.wireOp",EDGE,"E6.27.1"),sQuery(id+"F0.wireOp",EDGE,"E6.27.2"),sQuery(id+"F0.wireOp",EDGE,"E6.27.3"),sQuery(id+"F0.wireOp",EDGE,"E6.28.0"),sQuery(id+"F0.wireOp",EDGE,"E6.28.1"),sQuery(id+"F0.wireOp",EDGE,"E6.28.2"),sQuery(id+"F0.wireOp",EDGE,"E6.28.3"),sQuery(id+"F0.wireOp",EDGE,"E6.29.0"),sQuery(id+"F0.wireOp",EDGE,"E6.29.1"),sQuery(id+"F0.wireOp",EDGE,"E6.29.2"),sQuery(id+"F0.wireOp",EDGE,"E6.29.3")])],"isStart":false});
            var sketch = newSketch(context, id + "F4", { "sketchPlane" : qUnion([Q0])});
            skCircle(sketch, "E11", {"center": v(0, 0) * mm, "radius": 0.45 * mm});
            skLineSegment(sketch, "E12", {"start": v(0, 0) * mm, "end": v(0, 0.45) * mm, "construction": true});
            skLineSegment(sketch, "E13", {"start": v(-0.07, 0.45) * mm, "end": v(-0.06, 0.6) * mm});
            skLineSegment(sketch, "E14", {"start": v(-0.06, 0.6) * mm, "end": v(0, 0.6) * mm});
            skLineSegment(sketch, "E15", {"start": v(0, 0.6) * mm, "end": v(0.06, 0.6) * mm});
            skLineSegment(sketch, "E16", {"start": v(0.06, 0.6) * mm, "end": v(0.07, 0.45) * mm});
            skLineSegment(sketch, "E17.1.0", {"start": v(-0.4, 0.45) * mm, "end": v(-0.35, 0.48) * mm});
            skLineSegment(sketch, "E17.1.1", {"start": v(-0.35, 0.48) * mm, "end": v(-0.3, 0.52) * mm});
            skLineSegment(sketch, "E17.1.2", {"start": v(-0.3, 0.52) * mm, "end": v(-0.2, 0.4) * mm});
            skLineSegment(sketch, "E17.1.3", {"start": v(-0.32, 0.32) * mm, "end": v(-0.4, 0.45) * mm});
            skLineSegment(sketch, "E17.2.0", {"start": v(-0.58, 0.13) * mm, "end": v(-0.57, 0.18) * mm});
            skLineSegment(sketch, "E17.2.1", {"start": v(-0.57, 0.18) * mm, "end": v(-0.55, 0.24) * mm});
            skLineSegment(sketch, "E17.2.2", {"start": v(-0.55, 0.24) * mm, "end": v(-0.4, 0.2) * mm});
            skLineSegment(sketch, "E17.2.3", {"start": v(-0.45, 0.07) * mm, "end": v(-0.58, 0.13) * mm});
            skLineSegment(sketch, "E17.3.0", {"start": v(-0.55, -0.24) * mm, "end": v(-0.57, -0.18) * mm});
            skLineSegment(sketch, "E17.3.1", {"start": v(-0.57, -0.18) * mm, "end": v(-0.58, -0.13) * mm});
            skLineSegment(sketch, "E17.3.2", {"start": v(-0.58, -0.13) * mm, "end": v(-0.45, -0.07) * mm});
            skLineSegment(sketch, "E17.3.3", {"start": v(-0.4, -0.2) * mm, "end": v(-0.55, -0.24) * mm});
            skLineSegment(sketch, "E17.4.0", {"start": v(-0.3, -0.52) * mm, "end": v(-0.35, -0.48) * mm});
            skLineSegment(sketch, "E17.4.1", {"start": v(-0.35, -0.48) * mm, "end": v(-0.4, -0.45) * mm});
            skLineSegment(sketch, "E17.4.2", {"start": v(-0.4, -0.45) * mm, "end": v(-0.32, -0.32) * mm});
            skLineSegment(sketch, "E17.4.3", {"start": v(-0.2, -0.4) * mm, "end": v(-0.3, -0.52) * mm});
            skLineSegment(sketch, "E17.5.0", {"start": v(0.06, -0.6) * mm, "end": v(0, -0.6) * mm});
            skLineSegment(sketch, "E17.5.1", {"start": v(0, -0.6) * mm, "end": v(-0.06, -0.6) * mm});
            skLineSegment(sketch, "E17.5.2", {"start": v(-0.06, -0.6) * mm, "end": v(-0.07, -0.45) * mm});
            skLineSegment(sketch, "E17.5.3", {"start": v(0.07, -0.45) * mm, "end": v(0.06, -0.6) * mm});
            skLineSegment(sketch, "E17.6.0", {"start": v(0.4, -0.45) * mm, "end": v(0.35, -0.48) * mm});
            skLineSegment(sketch, "E17.6.1", {"start": v(0.35, -0.48) * mm, "end": v(0.3, -0.52) * mm});
            skLineSegment(sketch, "E17.6.2", {"start": v(0.3, -0.52) * mm, "end": v(0.2, -0.4) * mm});
            skLineSegment(sketch, "E17.6.3", {"start": v(0.32, -0.32) * mm, "end": v(0.4, -0.45) * mm});
            skLineSegment(sketch, "E17.7.0", {"start": v(0.58, -0.13) * mm, "end": v(0.57, -0.18) * mm});
            skLineSegment(sketch, "E17.7.1", {"start": v(0.57, -0.18) * mm, "end": v(0.55, -0.24) * mm});
            skLineSegment(sketch, "E17.7.2", {"start": v(0.55, -0.24) * mm, "end": v(0.4, -0.2) * mm});
            skLineSegment(sketch, "E17.7.3", {"start": v(0.45, -0.07) * mm, "end": v(0.58, -0.13) * mm});
            skLineSegment(sketch, "E18.1.8.0", {"start": v(0.55, 0.24) * mm, "end": v(0.57, 0.18) * mm});
            skLineSegment(sketch, "E18.3.8.0", {"start": v(0.57, 0.18) * mm, "end": v(0.58, 0.13) * mm});
            skLineSegment(sketch, "E18.6.8.0", {"start": v(0.58, 0.13) * mm, "end": v(0.45, 0.07) * mm});
            skLineSegment(sketch, "E18.9.8.0", {"start": v(0.4, 0.2) * mm, "end": v(0.55, 0.24) * mm});
            skLineSegment(sketch, "E19.1.9.0", {"start": v(0.3, 0.52) * mm, "end": v(0.35, 0.48) * mm});
            skLineSegment(sketch, "E19.3.9.0", {"start": v(0.35, 0.48) * mm, "end": v(0.4, 0.45) * mm});
            skLineSegment(sketch, "E19.6.9.0", {"start": v(0.4, 0.45) * mm, "end": v(0.32, 0.32) * mm});
            skLineSegment(sketch, "E19.9.9.0", {"start": v(0.2, 0.4) * mm, "end": v(0.3, 0.52) * mm});
            skSolve(sketch);
        }
        {
            var Q0;
            Q0 = qSketchRegion(id + "F4", true);
            extrude(context, id + "F5", {"entities" : qUnion([Q0]), "operationType" : NewBodyOperationType.ADD, "depth" : 0.8 * mm});
        }
        {
            var Q0;
            Q0=makeQuery(id+"F5.opExtrude","CAP_FACE",FACE,{"disambiguationData":[OSD([sQuery(id+"F4.wireOp",EDGE,"E11"),sQuery(id+"F4.wireOp",EDGE,"E13"),sQuery(id+"F4.wireOp",EDGE,"E14"),sQuery(id+"F4.wireOp",EDGE,"E15"),sQuery(id+"F4.wireOp",EDGE,"E16"),sQuery(id+"F4.wireOp",EDGE,"E17.1.0"),sQuery(id+"F4.wireOp",EDGE,"E17.1.1"),sQuery(id+"F4.wireOp",EDGE,"E17.1.2"),sQuery(id+"F4.wireOp",EDGE,"E17.1.3"),sQuery(id+"F4.wireOp",EDGE,"E17.2.0"),sQuery(id+"F4.wireOp",EDGE,"E17.2.1"),sQuery(id+"F4.wireOp",EDGE,"E17.2.2"),sQuery(id+"F4.wireOp",EDGE,"E17.2.3"),sQuery(id+"F4.wireOp",EDGE,"E17.3.0"),sQuery(id+"F4.wireOp",EDGE,"E17.3.1"),sQuery(id+"F4.wireOp",EDGE,"E17.3.2"),sQuery(id+"F4.wireOp",EDGE,"E17.3.3"),sQuery(id+"F4.wireOp",EDGE,"E17.4.0"),sQuery(id+"F4.wireOp",EDGE,"E17.4.1"),sQuery(id+"F4.wireOp",EDGE,"E17.4.2"),sQuery(id+"F4.wireOp",EDGE,"E17.4.3"),sQuery(id+"F4.wireOp",EDGE,"E17.5.0"),sQuery(id+"F4.wireOp",EDGE,"E17.5.1"),sQuery(id+"F4.wireOp",EDGE,"E17.5.2"),sQuery(id+"F4.wireOp",EDGE,"E17.5.3"),sQuery(id+"F4.wireOp",EDGE,"E17.6.0"),sQuery(id+"F4.wireOp",EDGE,"E17.6.1"),sQuery(id+"F4.wireOp",EDGE,"E17.6.2"),sQuery(id+"F4.wireOp",EDGE,"E17.6.3"),sQuery(id+"F4.wireOp",EDGE,"E17.7.0"),sQuery(id+"F4.wireOp",EDGE,"E17.7.1"),sQuery(id+"F4.wireOp",EDGE,"E17.7.2"),sQuery(id+"F4.wireOp",EDGE,"E17.7.3")])],"isStart":false});
            var sketch = newSketch(context, id + "F6", { "sketchPlane" : qUnion([Q0])});
            skCircle(sketch, "E20", {"center": v(0, 0) * mm, "radius": 0.1 * mm});
            skSolve(sketch);
        }
        {
            var Q0;
            Q0 = qSketchRegion(id + "F6", true);
            extrude(context, id + "F7", {"entities" : qUnion([Q0]), "operationType" : NewBodyOperationType.REMOVE, "oppositeDirection" : true, "depth" : 25 * mm});
        }
    });
